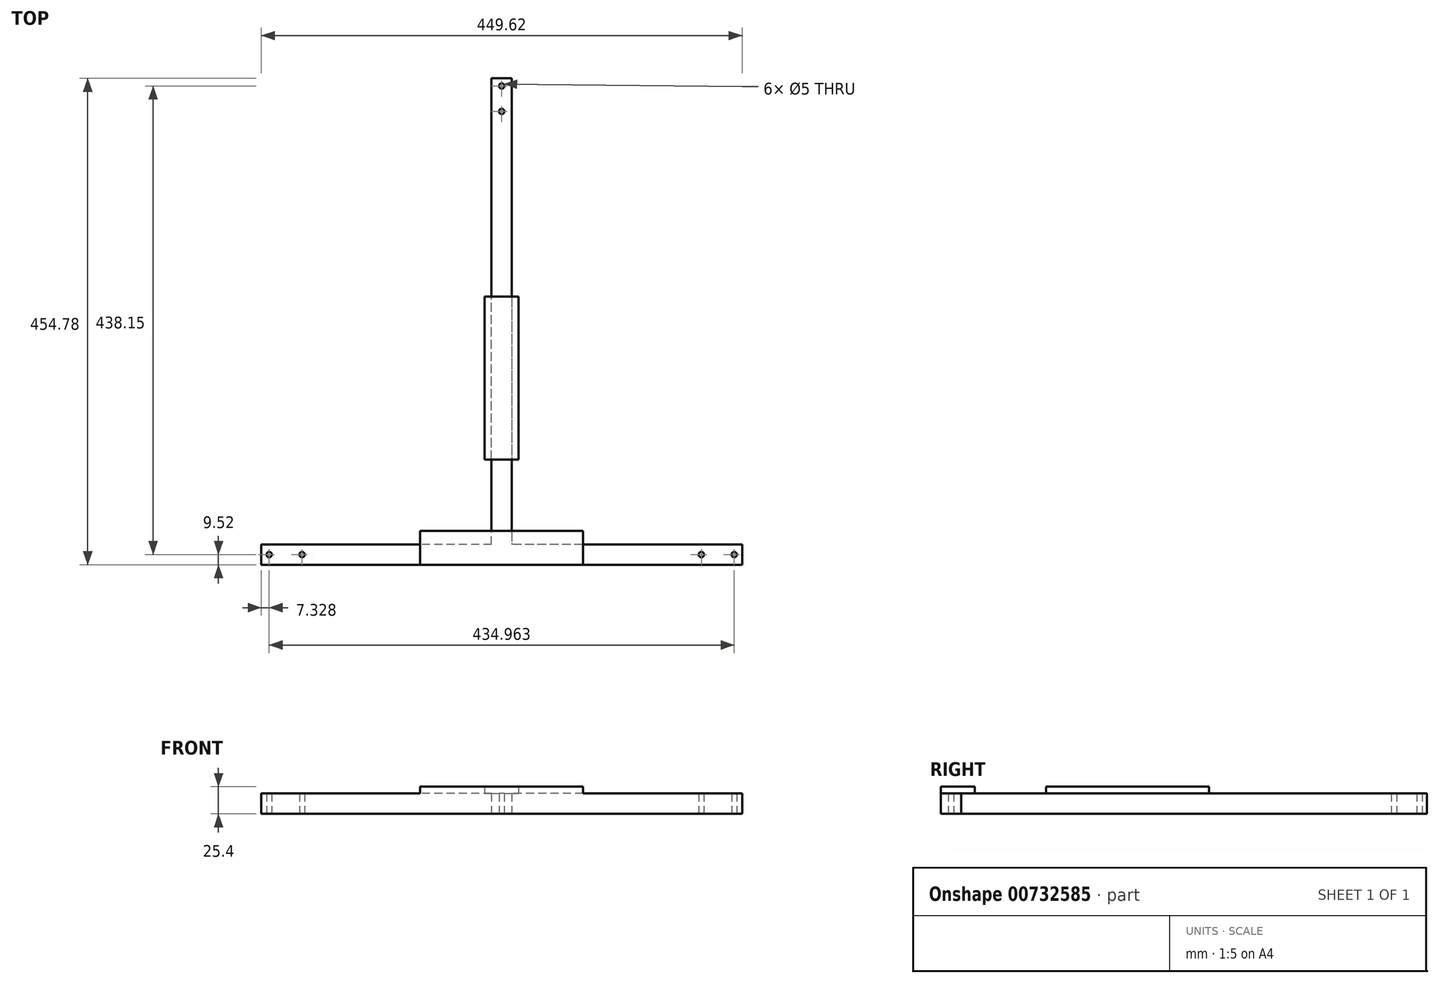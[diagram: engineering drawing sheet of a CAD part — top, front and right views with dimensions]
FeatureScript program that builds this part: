
annotation { "Feature Type Name" : "Feature", "Feature Type Description" : "" }
export const myFeature = defineFeature(function(context is Context, id is Id, definition is map)
    precondition{}
    {
        {
            var Q0;
            Q0=qCreatedBy(makeId("Top.planeOp"),FACE);
            var sketch = newSketch(context, id + "F0", { "sketchPlane" : qUnion([Q0])});
            skCircle(sketch, "E0", {"center": v(0, 0) * mm, "radius": 249.24 * mm, "construction": true});
            skLineSegment(sketch, "E1", {"start": v(-224.81, -155.57) * mm, "end": v(-224.81, -174.62) * mm});
            skLineSegment(sketch, "E2", {"start": v(-224.81, -174.62) * mm, "end": v(224.81, -174.62) * mm});
            skLineSegment(sketch, "E3", {"start": v(224.81, -174.62) * mm, "end": v(224.81, -155.57) * mm});
            skLineSegment(sketch, "E4", {"start": v(224.81, -155.57) * mm, "end": v(9.53, -155.57) * mm});
            skLineSegment(sketch, "E5", {"start": v(-9.52, -155.57) * mm, "end": v(-9.52, 280.16) * mm});
            skLineSegment(sketch, "E6", {"start": v(-9.52, 280.16) * mm, "end": v(9.52, 280.16) * mm});
            skLineSegment(sketch, "E7", {"start": v(9.52, 280.16) * mm, "end": v(9.53, -155.57) * mm});
            skPoint(sketch, "E8", {"position": v(0, 280.16) * mm});
            skPoint(sketch, "E9", {"position": v(0, -155.57) * mm});
            skLineSegment(sketch, "E10", {"start": v(-224.81, -165.1) * mm, "end": v(224.81, -165.1) * mm, "construction": true});
            skPoint(sketch, "E11", {"position": v(186.71, -165.1) * mm});
            skPoint(sketch, "E12", {"position": v(0, 249.24) * mm});
            skLineSegment(sketch, "E13.trimOffspring", {"start": v(-9.52, -155.57) * mm, "end": v(-224.81, -155.58) * mm});
            skPoint(sketch, "E14", {"position": v(-186.71, -165.1) * mm});
            skCircle(sketch, "E15", {"center": v(0, 0) * mm, "radius": 273.05 * mm, "construction": true});
            skPoint(sketch, "E16", {"position": v(0, 273.05) * mm});
            skPoint(sketch, "E17", {"position": v(-217.48, -165.1) * mm});
            skPoint(sketch, "E18", {"position": v(217.48, -165.1) * mm});
            skSolve(sketch);
        }
        {
            var Q0;
            Q0 = qSketchRegion(id + "F0", true);
            extrude(context, id + "F1", {"entities" : qUnion([Q0]), "depth" : 19.05 * mm, "offsetDistance" : 25.4 * mm});
        }
        {
            var Q0;
            Q0=makeQuery(id+"F1.opExtrude","CAP_FACE",FACE,{"disambiguationData":[OSD([sQuery(id+"F0.wireOp",EDGE,"E1"),sQuery(id+"F0.wireOp",EDGE,"E2"),sQuery(id+"F0.wireOp",EDGE,"E3"),sQuery(id+"F0.wireOp",EDGE,"E4"),sQuery(id+"F0.wireOp",EDGE,"E5"),sQuery(id+"F0.wireOp",EDGE,"E6"),sQuery(id+"F0.wireOp",EDGE,"E7"),sQuery(id+"F0.wireOp",EDGE,"E13.trimOffspring")])],"isStart":false});
            var sketch = newSketch(context, id + "F2", { "sketchPlane" : qUnion([Q0])});
            skLineSegment(sketch, "E19.bottom", {"start": v(-76.2, -174.62) * mm, "end": v(76.2, -174.62) * mm});
            skLineSegment(sketch, "E19.top", {"start": v(-76.2, -142.88) * mm, "end": v(76.2, -142.88) * mm});
            skLineSegment(sketch, "E19.left", {"start": v(-76.2, -174.62) * mm, "end": v(-76.2, -142.88) * mm});
            skLineSegment(sketch, "E19.right", {"start": v(76.2, -174.62) * mm, "end": v(76.2, -142.88) * mm});
            skLineSegment(sketch, "E20.bottom", {"start": v(-15.87, -76.2) * mm, "end": v(15.88, -76.2) * mm});
            skLineSegment(sketch, "E20.top", {"start": v(-15.87, 76.2) * mm, "end": v(15.87, 76.2) * mm});
            skLineSegment(sketch, "E20.left", {"start": v(-15.87, -76.2) * mm, "end": v(-15.87, 76.2) * mm});
            skLineSegment(sketch, "E20.right", {"start": v(15.88, -76.2) * mm, "end": v(15.87, 76.2) * mm});
            skLineSegment(sketch, "E21", {"start": v(15.88, 0) * mm, "end": v(0, 0) * mm, "construction": true});
            skSolve(sketch);
        }
        {
            var Q0;
            Q0 = qSketchRegion(id + "F2", true);
            extrude(context, id + "F3", {"entities" : qUnion([Q0]), "operationType" : NewBodyOperationType.ADD, "depth" : 6.35 * mm, "offsetDistance" : 25.4 * mm});
        }
        {
            var Q0;
            Q0=sQuery(id+"F0.wireOp",VERTEX,"E11");
            var Q1;
            Q1=sQuery(id+"F0.wireOp",VERTEX,"E12");
            var Q2;
            Q2=sQuery(id+"F0.wireOp",VERTEX,"E14");
            var Q3;
            Q3=sQuery(id+"F0.wireOp",VERTEX,"E17");
            var Q4;
            Q4=sQuery(id+"F0.wireOp",VERTEX,"E18");
            var Q5;
            Q5=sQuery(id+"F0.wireOp",VERTEX,"E16");
            var Q6;
            Q6=makeQuery(id+"F1.opExtrude","SWEPT_BODY",BODY,{"disambiguationData":[OSD([sQuery(id+"F0.wireOp",EDGE,"E1"),sQuery(id+"F0.wireOp",EDGE,"E2"),sQuery(id+"F0.wireOp",EDGE,"E3"),sQuery(id+"F0.wireOp",EDGE,"E4"),sQuery(id+"F0.wireOp",EDGE,"E5"),sQuery(id+"F0.wireOp",EDGE,"E6"),sQuery(id+"F0.wireOp",EDGE,"E7"),sQuery(id+"F0.wireOp",EDGE,"E13.trimOffspring")])]});
            hole(context, id + "F4", {"style" : HoleStyle.SIMPLE, "endStyle" : HoleEndStyle.THROUGH, "oppositeDirection" : true, "standardTappedOrClearance" : lookupTablePath({ "standard" : "ISO", "engagement" : "75%", "pitch" : "1 mm", "size" : "M6", "type" : "Tapped" }), "standardBlindInLast" : lookupTablePath({ "standard" : "ISO", "engagement" : "75%", "pitch" : "1 mm", "size" : "M6", "type" : "Tapped" }), "holeDiameter" : 5 * mm, "majorDiameter" : 6 * mm, "showTappedDepth" : true, "isTappedThrough" : true, "tappedDepth" : 12.7 * mm, "tapClearance" : 3, "locations" : qUnion([Q0, Q1, Q2, Q3, Q4, Q5]), "scope" : qUnion([Q6])});
        }
    });
